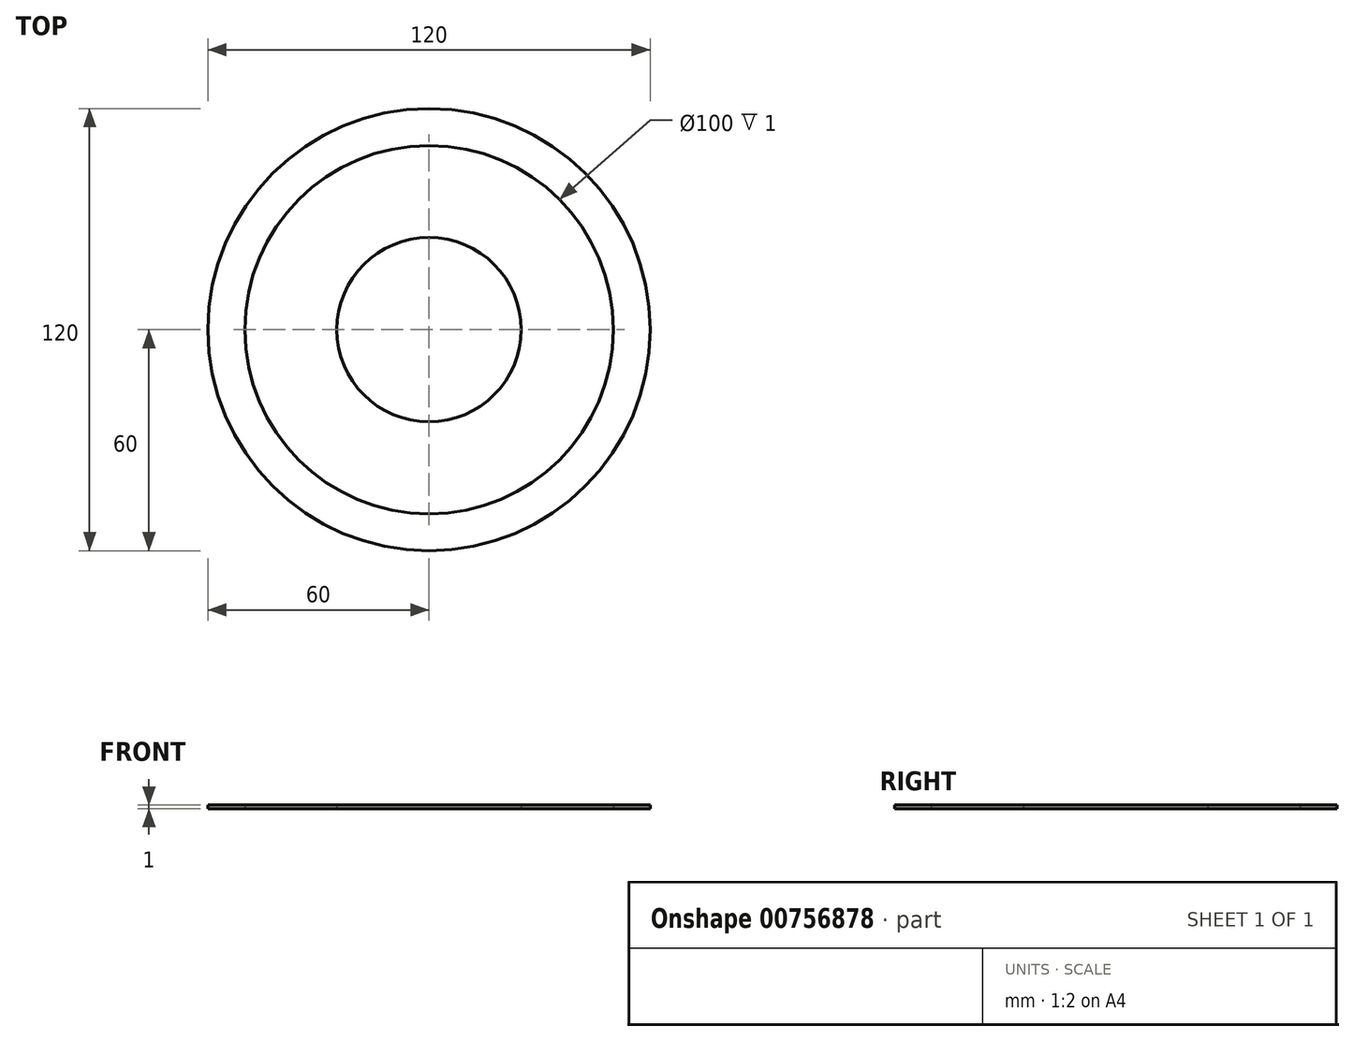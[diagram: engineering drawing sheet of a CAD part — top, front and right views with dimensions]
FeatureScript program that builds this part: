
annotation { "Feature Type Name" : "Feature", "Feature Type Description" : "" }
export const myFeature = defineFeature(function(context is Context, id is Id, definition is map)
    precondition{}
    {
        {
            var Q0;
            Q0=qCreatedBy(makeId("Top.planeOp"),FACE);
            var sketch = newSketch(context, id + "F0", { "sketchPlane" : qUnion([Q0])});
            skCircle(sketch, "E0", {"center": v(0, 0) * mm, "radius": 60 * mm});
            skCircle(sketch, "E1", {"center": v(0, 0) * mm, "radius": 25 * mm});
            skCircle(sketch, "E2", {"center": v(0, 0) * mm, "radius": 50 * mm});
            skSolve(sketch);
        }
        {
            var Q0;
            Q0=makeQuery(id+"F0.imprint","IMPRINT",FACE,{"disambiguationData":[TD([[makeQuery(id+"F0.imprint","IMPRINT",EDGE,{"derivedFrom":sQuery(id+"F0.wireOp",EDGE,"E0")}),1.0]])]});
            var Q1;
            Q1=makeQuery(id+"F0.imprint","IMPRINT",FACE,{"disambiguationData":[TD([[makeQuery(id+"F0.imprint","IMPRINT",EDGE,{"derivedFrom":sQuery(id+"F0.wireOp",EDGE,"E1")}),1.0]])]});
            var Q2;
            Q2=qSketchRegion(id+"F0",true);
            extrude(context, id + "F1", {"entities" : qUnion([Q0, Q1, Q2]), "depth" : 1 * mm});
        }
    });
